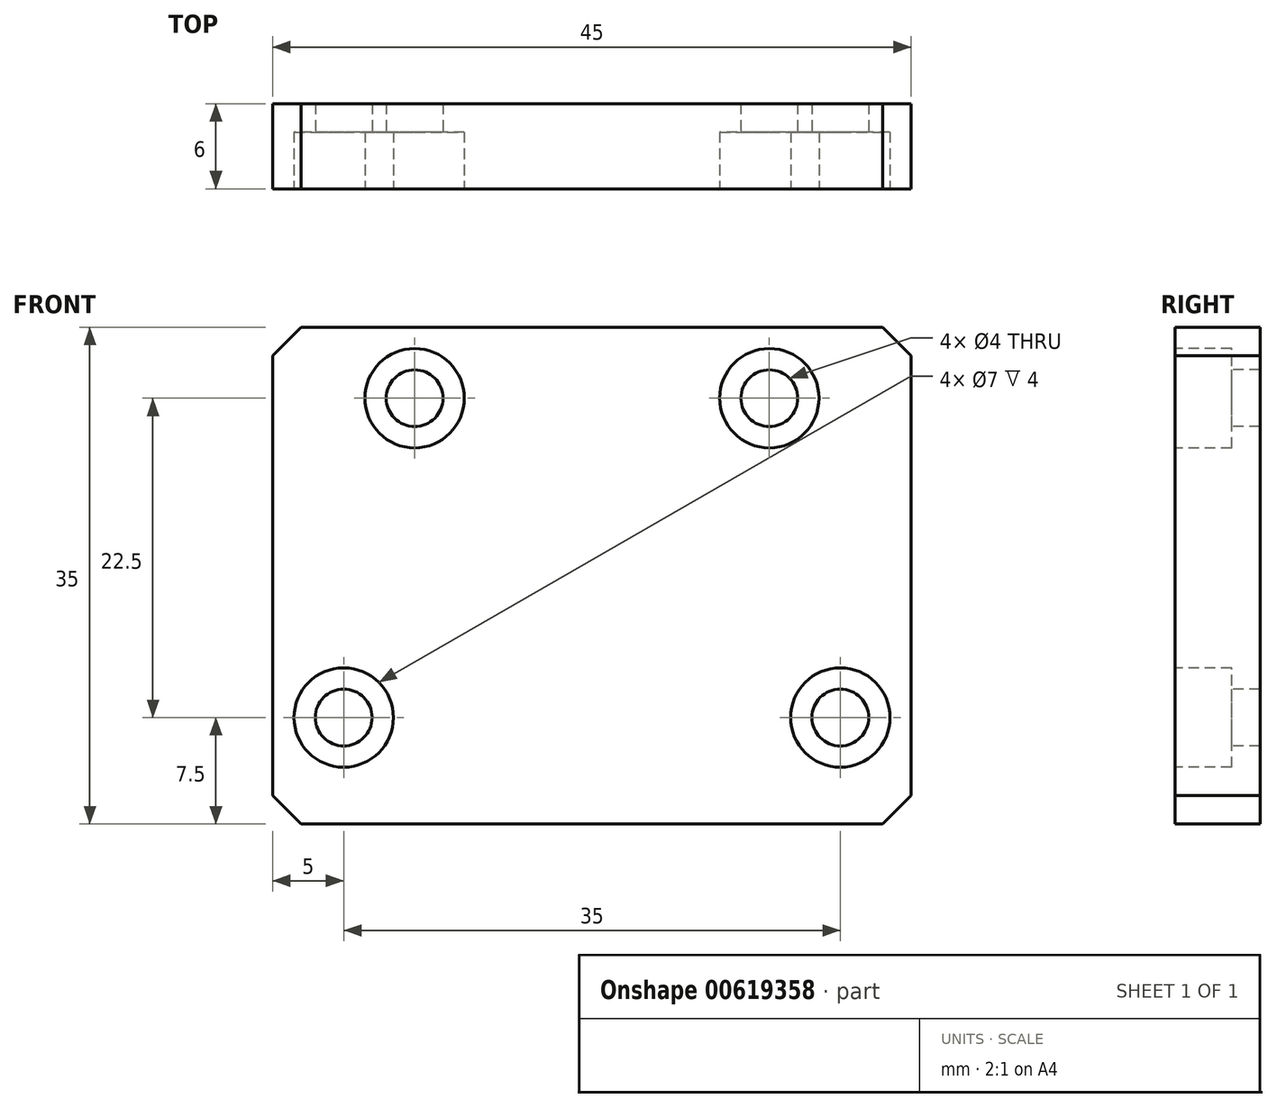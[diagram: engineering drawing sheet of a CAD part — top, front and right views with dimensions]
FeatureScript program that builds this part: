
annotation { "Feature Type Name" : "Feature", "Feature Type Description" : "" }
export const myFeature = defineFeature(function(context is Context, id is Id, definition is map)
    precondition{}
    {
        {
            var Q0;
            Q0=qCreatedBy(makeId("Front.planeOp"),FACE);
            var sketch = newSketch(context, id + "F0", { "sketchPlane" : qUnion([Q0])});
            skLineSegment(sketch, "E0.bottom", {"start": v(-22.5, 20) * mm, "end": v(22.5, 20) * mm});
            skLineSegment(sketch, "E0.top", {"start": v(-22.5, -15) * mm, "end": v(22.5, -15) * mm});
            skLineSegment(sketch, "E0.left", {"start": v(-22.5, 20) * mm, "end": v(-22.5, -15) * mm});
            skLineSegment(sketch, "E0.right", {"start": v(22.5, 20) * mm, "end": v(22.5, -15) * mm});
            skSolve(sketch);
        }
        {
            var Q0;
            Q0=makeQuery(id+"F0.imprint","IMPRINT",FACE,{"disambiguationData":[TD([[makeQuery(id+"F0.imprint","IMPRINT",EDGE,{"derivedFrom":sQuery(id+"F0.wireOp",EDGE,"E0.bottom")}),-1.0]])]});
            extrude(context, id + "F1", {"entities" : qUnion([Q0]), "depth" : 4.5 * mm, "offsetDistance" : 25 * mm});
        }
        {
            var Q0;
            Q0=makeQuery(id+"F1.opExtrude","SWEPT_FACE",FACE,{"disambiguationData":[OSD([sQuery(id+"F0.wireOp",EDGE,"E0.bottom")])]});
            var sketch = newSketch(context, id + "F2", { "sketchPlane" : qUnion([Q0])});
            skLineSegment(sketch, "E1.bottom", {"start": v(-10, -1.5) * mm, "end": v(5, -1.5) * mm});
            skLineSegment(sketch, "E1.top", {"start": v(-10, -3) * mm, "end": v(5, -3) * mm});
            skLineSegment(sketch, "E1.left", {"start": v(-10, -1.5) * mm, "end": v(-10, -3) * mm});
            skLineSegment(sketch, "E1.right", {"start": v(5, -1.5) * mm, "end": v(5, -3) * mm});
            skPoint(sketch, "E1.middle.positionSnap0", {"position": v(22.5, -2.25) * mm});
            skPoint(sketch, "E1.centerSnap0", {"position": v(22.5, -2.25) * mm});
            skSolve(sketch);
        }
        {
            var Q0;
            Q0=qSketchRegion(id+"F2",true);
            extrude(context, id + "F3", {"entities" : qUnion([Q0]), "operationType" : NewBodyOperationType.REMOVE, "endBound" : BoundingType.THROUGH_ALL, "oppositeDirection" : true, "depth" : 25 * mm, "offsetDistance" : 25 * mm});
        }
        {
            var Q0;
            Q0=makeQuery(id+"F1.opExtrude","CAP_FACE",FACE,{"disambiguationData":[OSD([sQuery(id+"F0.wireOp",EDGE,"E0.bottom"),sQuery(id+"F0.wireOp",EDGE,"E0.top"),sQuery(id+"F0.wireOp",EDGE,"E0.left"),sQuery(id+"F0.wireOp",EDGE,"E0.right")])],"isStart":false});
            var sketch = newSketch(context, id + "F4", { "sketchPlane" : qUnion([Q0])});
            skCircle(sketch, "E2", {"center": v(17.5, -7.5) * mm, "radius": 1.75 * mm});
            skCircle(sketch, "E3.MirrorC", {"center": v(-17.5, -7.5) * mm, "radius": 1.75 * mm});
            skSolve(sketch);
        }
        {
            var Q0;
            Q0=qSketchRegion(id+"F4",true);
            extrude(context, id + "F5", {"entities" : qUnion([Q0]), "operationType" : NewBodyOperationType.REMOVE, "oppositeDirection" : true, "depth" : 3.5 * mm, "offsetDistance" : 25 * mm});
        }
        {
            var Q0;
            Q0=makeQuery(id+"F1.opExtrude","CAP_FACE",FACE,{"disambiguationData":[OSD([sQuery(id+"F0.wireOp",EDGE,"E0.bottom"),sQuery(id+"F0.wireOp",EDGE,"E0.top"),sQuery(id+"F0.wireOp",EDGE,"E0.left"),sQuery(id+"F0.wireOp",EDGE,"E0.right")])],"isStart":false});
            var sketch = newSketch(context, id + "F6", { "sketchPlane" : qUnion([Q0])});
            skPoint(sketch, "E4", {"position": v(17.5, -7.5) * mm});
            skPoint(sketch, "E5", {"position": v(-17.5, -7.5) * mm});
            skCircle(sketch, "E6", {"center": v(17.5, -7.5) * mm, "radius": 2 * mm});
            skCircle(sketch, "E7", {"center": v(-17.5, -7.5) * mm, "radius": 2 * mm});
            skSolve(sketch);
        }
        {
            var Q0;
            Q0=qSketchRegion(id+"F6",true);
            extrude(context, id + "F7", {"entities" : qUnion([Q0]), "operationType" : NewBodyOperationType.REMOVE, "endBound" : BoundingType.THROUGH_ALL, "oppositeDirection" : true, "depth" : 25 * mm, "offsetDistance" : 25 * mm});
        }
        {
            var Q0;
            Q0=makeQuery(id+"F1.opExtrude","CAP_FACE",FACE,{"disambiguationData":[OSD([sQuery(id+"F0.wireOp",EDGE,"E0.bottom"),sQuery(id+"F0.wireOp",EDGE,"E0.top"),sQuery(id+"F0.wireOp",EDGE,"E0.left"),sQuery(id+"F0.wireOp",EDGE,"E0.right")])],"isStart":true});
            var sketch = newSketch(context, id + "F8", { "sketchPlane" : qUnion([Q0])});
            skLineSegment(sketch, "E8.bottom", {"start": v(10, 5) * mm, "end": v(0, 5) * mm});
            skLineSegment(sketch, "E8.top", {"start": v(10, 15) * mm, "end": v(0, 15) * mm});
            skLineSegment(sketch, "E8.left", {"start": v(10, 5) * mm, "end": v(10, 15) * mm});
            skLineSegment(sketch, "E8.right", {"start": v(0, 5) * mm, "end": v(0, 15) * mm});
            skPoint(sketch, "E8.middle", {"position": v(0, 7) * mm});
            skSolve(sketch);
        }
        {
            var Q0;
            Q0=qSketchRegion(id+"F8",true);
            extrude(context, id + "F9", {"entities" : qUnion([Q0]), "operationType" : NewBodyOperationType.REMOVE, "oppositeDirection" : true, "depth" : 3 * mm, "offsetDistance" : 25 * mm});
        }
        {
            var Q0;
            Q0=makeQuery(id+"F1.opExtrude","SWEPT_EDGE",EDGE,{"disambiguationData":[OSD([sQuery(id+"F0.wireOp",EDGE,"E0.bottom"),sQuery(id+"F0.wireOp",EDGE,"E0.left")])]});
            var Q1;
            Q1=makeQuery(id+"F1.opExtrude","SWEPT_EDGE",EDGE,{"disambiguationData":[OSD([sQuery(id+"F0.wireOp",EDGE,"E0.bottom"),sQuery(id+"F0.wireOp",EDGE,"E0.right")])]});
            var Q2;
            Q2=makeQuery(id+"F1.opExtrude","SWEPT_EDGE",EDGE,{"disambiguationData":[OSD([sQuery(id+"F0.wireOp",EDGE,"E0.top"),sQuery(id+"F0.wireOp",EDGE,"E0.right")])]});
            var Q3;
            Q3=makeQuery(id+"F1.opExtrude","SWEPT_EDGE",EDGE,{"disambiguationData":[OSD([sQuery(id+"F0.wireOp",EDGE,"E0.top"),sQuery(id+"F0.wireOp",EDGE,"E0.left")])]});
            chamfer(context, id + "F10", {"entities" : qUnion([Q0, Q1, Q2, Q3]), "width" : 2 * mm, "tangentPropagation" : true});
        }
        {
            var Q0;
            Q0=makeQuery(id+"F1.opExtrude","SWEPT_FACE",FACE,{"disambiguationData":[OSD([sQuery(id+"F0.wireOp",EDGE,"E0.top")])]});
            var sketch = newSketch(context, id + "F11", { "sketchPlane" : qUnion([Q0])});
            skPoint(sketch, "E9.oppositeSnap0", {"position": v(0, 0) * mm});
            skLineSegment(sketch, "E9.bottom", {"start": v(-23.92, 3) * mm, "end": v(24.43, 3) * mm});
            skLineSegment(sketch, "E9.top", {"start": v(-23.92, 0) * mm, "end": v(24.43, 0) * mm});
            skLineSegment(sketch, "E9.left", {"start": v(-23.92, 3) * mm, "end": v(-23.92, 0) * mm});
            skLineSegment(sketch, "E9.right", {"start": v(24.43, 3) * mm, "end": v(24.43, 0) * mm});
            skSolve(sketch);
        }
        {
            var Q0;
            Q0 = qSketchRegion(id + "F11", true);
            extrude(context, id + "F12", {"entities" : qUnion([Q0]), "operationType" : NewBodyOperationType.REMOVE, "endBound" : BoundingType.THROUGH_ALL, "oppositeDirection" : true, "depth" : 25 * mm, "offsetDistance" : 25 * mm});
        }
        {
            var Q0;
            Q0=makeQuery(id+"F1.opExtrude","CAP_FACE",FACE,{"disambiguationData":[OSD([sQuery(id+"F0.wireOp",EDGE,"E0.bottom"),sQuery(id+"F0.wireOp",EDGE,"E0.top"),sQuery(id+"F0.wireOp",EDGE,"E0.left"),sQuery(id+"F0.wireOp",EDGE,"E0.right")])],"isStart":false});
            var sketch = newSketch(context, id + "F13", { "sketchPlane" : qUnion([Q0])});
            skLineSegment(sketch, "E10.0", {"start": v(-22.5, 20) * mm, "end": v(22.5, 20) * mm});
            skLineSegment(sketch, "E10.1", {"start": v(-22.5, 20) * mm, "end": v(-22.5, -15) * mm});
            skLineSegment(sketch, "E10.2", {"start": v(-22.5, -15) * mm, "end": v(22.5, -15) * mm});
            skLineSegment(sketch, "E10.3", {"start": v(22.5, 20) * mm, "end": v(22.5, -15) * mm});
            skSolve(sketch);
        }
        {
            var Q0;
            Q0 = qSketchRegion(id + "F13", true);
            extrude(context, id + "F14", {"entities" : qUnion([Q0]), "operationType" : NewBodyOperationType.ADD, "depth" : 4.5 * mm, "offsetDistance" : 25 * mm});
        }
        {
            var Q0;
            Q0=makeQuery(id+"F14.opExtrude","SWEPT_EDGE",EDGE,{"disambiguationData":[OSD([sQuery(id+"F13.wireOp",EDGE,"E10.1"),sQuery(id+"F13.wireOp",EDGE,"E10.2")])]});
            var Q1;
            Q1=makeQuery(id+"F14.opExtrude","SWEPT_EDGE",EDGE,{"disambiguationData":[OSD([sQuery(id+"F13.wireOp",EDGE,"E10.2"),sQuery(id+"F13.wireOp",EDGE,"E10.3")])]});
            var Q2;
            Q2=makeQuery(id+"F14.opExtrude","SWEPT_EDGE",EDGE,{"disambiguationData":[OSD([sQuery(id+"F13.wireOp",EDGE,"E10.0"),sQuery(id+"F13.wireOp",EDGE,"E10.3")])]});
            var Q3;
            Q3=makeQuery(id+"F14.opExtrude","SWEPT_EDGE",EDGE,{"disambiguationData":[OSD([sQuery(id+"F13.wireOp",EDGE,"E10.0"),sQuery(id+"F13.wireOp",EDGE,"E10.1")])]});
            chamfer(context, id + "F15", {"entities" : qUnion([Q0, Q1, Q2, Q3]), "width" : 2 * mm, "tangentPropagation" : true});
        }
        {
            var Q0;
            Q0=makeQuery(id+"F12.boolean.opBoolean","MERGE",FACE,{"derivedFrom":[makeQuery(id+"F3.boolean.opBoolean","COPY",FACE,{"derivedFrom":makeQuery(id+"F3.opExtrude","SWEPT_FACE",FACE,{"disambiguationData":[OSD([sQuery(id+"F2.wireOp",EDGE,"E1.top")])]})}),makeQuery(id+"F12.opExtrude","SWEPT_FACE",FACE,{"disambiguationData":[OSD([sQuery(id+"F11.wireOp",EDGE,"E9.bottom")])]})]});
            var sketch = newSketch(context, id + "F16", { "sketchPlane" : qUnion([Q0])});
            skCircle(sketch, "E11.0", {"center": v(17.5, -7.5) * mm, "radius": 2 * mm});
            skCircle(sketch, "E12.0", {"center": v(-17.5, -7.5) * mm, "radius": 2 * mm});
            skSolve(sketch);
        }
        {
            var Q0;
            Q0 = qSketchRegion(id + "F16", true);
            extrude(context, id + "F17", {"entities" : qUnion([Q0]), "operationType" : NewBodyOperationType.REMOVE, "endBound" : BoundingType.THROUGH_ALL, "oppositeDirection" : true, "depth" : 25 * mm, "offsetDistance" : 25 * mm});
        }
        {
            var Q0;
            Q0=makeQuery(id+"F14.opExtrude","CAP_FACE",FACE,{"disambiguationData":[OSD([sQuery(id+"F13.wireOp",EDGE,"E10.0"),sQuery(id+"F13.wireOp",EDGE,"E10.1"),sQuery(id+"F13.wireOp",EDGE,"E10.2"),sQuery(id+"F13.wireOp",EDGE,"E10.3")])],"isStart":false});
            var sketch = newSketch(context, id + "F18", { "sketchPlane" : qUnion([Q0])});
            skCircle(sketch, "E13", {"center": v(-17.5, -7.5) * mm, "radius": 3.5 * mm});
            skCircle(sketch, "E14", {"center": v(17.5, -7.5) * mm, "radius": 3.5 * mm});
            skSolve(sketch);
        }
        {
            var Q0;
            Q0 = qSketchRegion(id + "F18", true);
            extrude(context, id + "F19", {"entities" : qUnion([Q0]), "operationType" : NewBodyOperationType.REMOVE, "oppositeDirection" : true, "depth" : 4 * mm, "offsetDistance" : 25 * mm});
        }
        {
            var Q0;
            Q0=makeQuery(id+"F14.opExtrude","CAP_FACE",FACE,{"disambiguationData":[OSD([sQuery(id+"F13.wireOp",EDGE,"E10.0"),sQuery(id+"F13.wireOp",EDGE,"E10.1"),sQuery(id+"F13.wireOp",EDGE,"E10.2"),sQuery(id+"F13.wireOp",EDGE,"E10.3")])],"isStart":false});
            var sketch = newSketch(context, id + "F20", { "sketchPlane" : qUnion([Q0])});
            skCircle(sketch, "E15", {"center": v(-12.5, 15) * mm, "radius": 3.5 * mm});
            skCircle(sketch, "E16.MirrorC", {"center": v(12.5, 15) * mm, "radius": 3.5 * mm});
            skSolve(sketch);
        }
        {
            var Q0;
            Q0 = qSketchRegion(id + "F20", true);
            extrude(context, id + "F21", {"entities" : qUnion([Q0]), "operationType" : NewBodyOperationType.REMOVE, "oppositeDirection" : true, "depth" : 4 * mm, "offsetDistance" : 25 * mm});
        }
        {
            var Q0;
            Q0=makeQuery(id+"F14.opExtrude","CAP_FACE",FACE,{"disambiguationData":[OSD([sQuery(id+"F13.wireOp",EDGE,"E10.0"),sQuery(id+"F13.wireOp",EDGE,"E10.1"),sQuery(id+"F13.wireOp",EDGE,"E10.2"),sQuery(id+"F13.wireOp",EDGE,"E10.3")])],"isStart":false});
            var sketch = newSketch(context, id + "F22", { "sketchPlane" : qUnion([Q0])});
            skCircle(sketch, "E17", {"center": v(-12.5, 15) * mm, "radius": 2 * mm});
            skCircle(sketch, "E18", {"center": v(12.5, 15) * mm, "radius": 2 * mm});
            skSolve(sketch);
        }
        {
            var Q0;
            Q0 = qSketchRegion(id + "F22", true);
            extrude(context, id + "F23", {"entities" : qUnion([Q0]), "operationType" : NewBodyOperationType.REMOVE, "endBound" : BoundingType.THROUGH_ALL, "oppositeDirection" : true, "depth" : 25 * mm, "offsetDistance" : 25 * mm});
        }
    });
